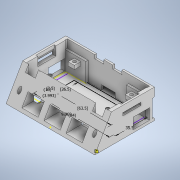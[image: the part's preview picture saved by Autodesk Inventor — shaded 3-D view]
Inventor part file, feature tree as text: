
AUTODESK INVENTOR PART (.ipt)
format: ipt  version: 2021 (Build 250183000, 183)  size: 610,816 bytes
history: native  units: mm
features: extrude x26, sketch x26, thread x2, projected_geometry x2, other x1, fillet x1
ambient origin geometry x8: Origin, YZ Plane, XZ Plane, XY Plane, X Axis, Y Axis, Z Axis, Center Point
bodies: Body1 (feature_tree)
feature tree (58):
  other  "Sólido1"
  extrude  "Extrusion Base"  Depth=2.0mm TaperAngle=0.0deg
  extrude  "Extrusión Angulo parte de adelante"  Depth=100.0mm TaperAngle=0.0deg
  extrude  "parte trasera diseño"  Depth=30.0mm TaperAngle=0.0deg
  extrude  "Extrusión parte trasera diseño con empalmes"  Depth=23.0mm
  fillet  "Empalme parte trasera diseño"  Radius=19.0mm
  extrude  "Parte delantera de la parte trasera diseño"  Depth=2.0mm
  extrude  "Extrusión Parte delantera de la parte trasera del diseño"  Depth=2.5mm
  extrude  "Extrusión Parte Trasera De la Parte trasera diseño"  Depth=2.5mm
  extrude  "Grado de inclinacion de 60.5 de parte delantera"  Depth=67.77mm TaperAngle=0.0deg
  extrude  "Lateral derecha de diseño"  Depth=10.0mm
  extrude  "Parte delantera diseño"  Depth=2.0mm
  extrude  "Lateral izquierda diseño"  Depth=4.0mm TaperAngle=0.0deg
  extrude  "Extrusion para placa trasera"  Depth=4.0mm
  extrude  "Extrusion capa parte delantera"  Depth=30.0mm
  extrude  "Extrusión huecos tornillos parte delantera"  Depth=22.142992mm
  extrude  "Tornillos Placa"  Depth=7.5mm TaperAngle=0.0deg
  thread  "Rosca1"  [1 undecoded]
  thread  "Rosca2"  [1 undecoded]
  extrude  "Extrusión sensores laterales"  Depth=3.5mm TaperAngle=0.0deg
  extrude  "Extrusión agujero cables inferiores"  Depth=30.0mm
  extrude  "Extrusión sensores delanteros"  Depth=4.5mm
  extrude  "Extrusión pads tornillos traseros placa"  Depth=30.0mm TaperAngle=0.0deg
  extrude  "Extrusión tornillos"  Depth=3.0mm
  sketch  "Boceto placa"  dims[d143=59.5mm d144=18.0mm d145=12.0mm d146=1.0mm d147=11.5mm d148=1.0mm d149=12.0mm d150=18.0mm d151=6.4mm d152=6.4mm d153=1.0mm d154=18.0mm d155=12.0mm d156=19.25mm d157=0.0mm d158=18.0mm d159=4.0mm d160=7.0mm d161=10.0mm d162=7.0mm d163=0.0mm d164=3.5mm d165=4.75mm d166=0.0mm d167=63.5mm d168=26.5mm d172=84.0mm d176=10.0mm d177=3.993mm d178=3.5mm d179=35.5mm d180=9.069006mm d181=15.0mm d182=20.0mm d183=12.562006mm d184=2.0mm d185=2.0mm d186=10.0mm d187=0.0mm d188=0.0mm d189=0.0mm d190=3.0mm d191=0.0mm d192=123.5mm d193=0.0mm d194=20.0mm d195=0.0mm d198=13.0mm d199=64.0mm d200=13.0mm d201=1.0mm d202=9.5mm d203=7.0mm d204=0.0mm d210=0.0mm d219=87.0mm d220=21.0mm d221=12.0mm d222=23.0mm d223=98.0mm d224=7.5mm d225=7.5mm d226=79.5mm d229=2.1mm d230=9.0mm d231=11.0mm d232=16.0mm d235=1.0mm d236=3.6mm d239=2.1mm d241=1.3mm d242=5.0mm d243=36.0mm d244=9.5mm d245=5.0mm d246=17.0mm d247=10.0mm d252=8.7mm d254=4.3mm d255=4.0mm d256=11.0mm d257=54.0mm d258=2.85mm d259=11.0mm d262=2.2mm d263=1.3mm d264=4.3mm d265=85.25mm d266=0.0mm d268=2.0mm d269=0.0mm d270=2.15mm d271=1.0mm d105=0.5mm d106=0.872665mm d107=0.5mm d108=0.872665mm d248=0.5mm d249=0.872665mm d250=0.5mm d251=0.872665mm d253=0.872665mm d272=0.5mm d273=0.872665mm]
  extrude  "Extrusión24"  Depth=18.0mm
  extrude  "Extrusión25"  Depth=12.0mm TaperAngle=0.0deg
  extrude  "Extrusión26"  Depth=5.0mm
  extrude  "Extrusión pared bateria"  Depth=18.5mm
  extrude  "Extrusión arreglo sensores"  Depth=3.0mm TaperAngle=0.0deg
  extrude  "Extrusión desnivel sensores"  Depth=18.0mm
  sketch  "Boceto2"  dims[d6=3.5mm d22=2.0mm d23=0.0mm]
  sketch  "Boceto4"  dims[d24=20.935224mm d25=100.0mm d26=0.0mm]
  sketch  "Boceto5"  dims[d27=4.5mm d28=30.0mm d29=0.0mm]
  sketch  "Boceto6"  dims[d30=3.33mm d31=23.0mm d32=19.0mm]
  sketch  "Boceto7"  dims[d33=2.5mm d34=0.0mm d35=2.0mm]
  sketch  "Boceto8"  dims[d36=26.615mm d37=2.5mm]
  sketch  "Boceto9"  dims[d38=30.0mm d39=0.0mm d40=2.5mm]
  sketch  "Boceto10"  dims[d41=21.0mm d42=67.77mm d43=23.15mm d44=0.0mm d45=0.0mm]
  sketch  "Boceto11"  dims[d46=34.0mm d47=10.0mm]
  projected_geometry  "Contorno proyectado1"
  sketch  "Boceto13"  dims[d48=2.0mm d49=2.0mm]
  sketch  "Boceto14"  dims[d50=4.0mm d51=0.0mm d52=4.0mm d53=0.0mm]
  sketch  "Boceto15"  dims[d54=4.0mm d55=0.0mm d56=4.0mm]
  projected_geometry  "Contorno proyectado2"
  sketch  "Boceto17"  dims[d57=30.0mm d58=0.0mm d59=10.480702mm]
  sketch  "Boceto24"  dims[d60=103.25mm d61=0.0mm d62=22.142992mm]
  sketch  "Boceto25"  dims[d63=57.5mm d64=0.0mm d65=93.0mm d66=0.0mm d67=7.5mm d68=7.5mm]
  sketch  "Boceto26"  dims[d69=3.5mm d70=90.25mm d71=0.0mm]
  sketch  "Boceto27"  dims[d120=13.0mm d121=30.0mm]
  sketch  "Boceto28"  dims[d122=3.5mm d123=4.5mm]
  sketch  "Boceto29"  dims[d124=18.0mm d125=0.0mm d126=30.0mm d127=0.0mm]
  sketch  "Boceto32"  dims[d128=30.0mm d129=0.0mm d130=3.0mm]
  sketch  "Boceto33"  dims[d131=3.0mm d132=18.0mm]
  sketch  "Boceto34"  dims[d133=12.0mm d134=98.25mm d135=0.0mm]
  sketch  "Boceto36"  dims[d136=15.0mm d137=5.0mm]
  sketch  "Boceto39"  dims[d138=0.0mm d139=18.5mm]
  sketch  "Boceto40"  dims[d140=18.5mm d141=3.0mm d142=0.0mm]
note: 2 required parameter values undecoded (feature->parameter linkage not recoverable at this tier; creation-order binding heuristic only, values carry confidence <= 0.55)
